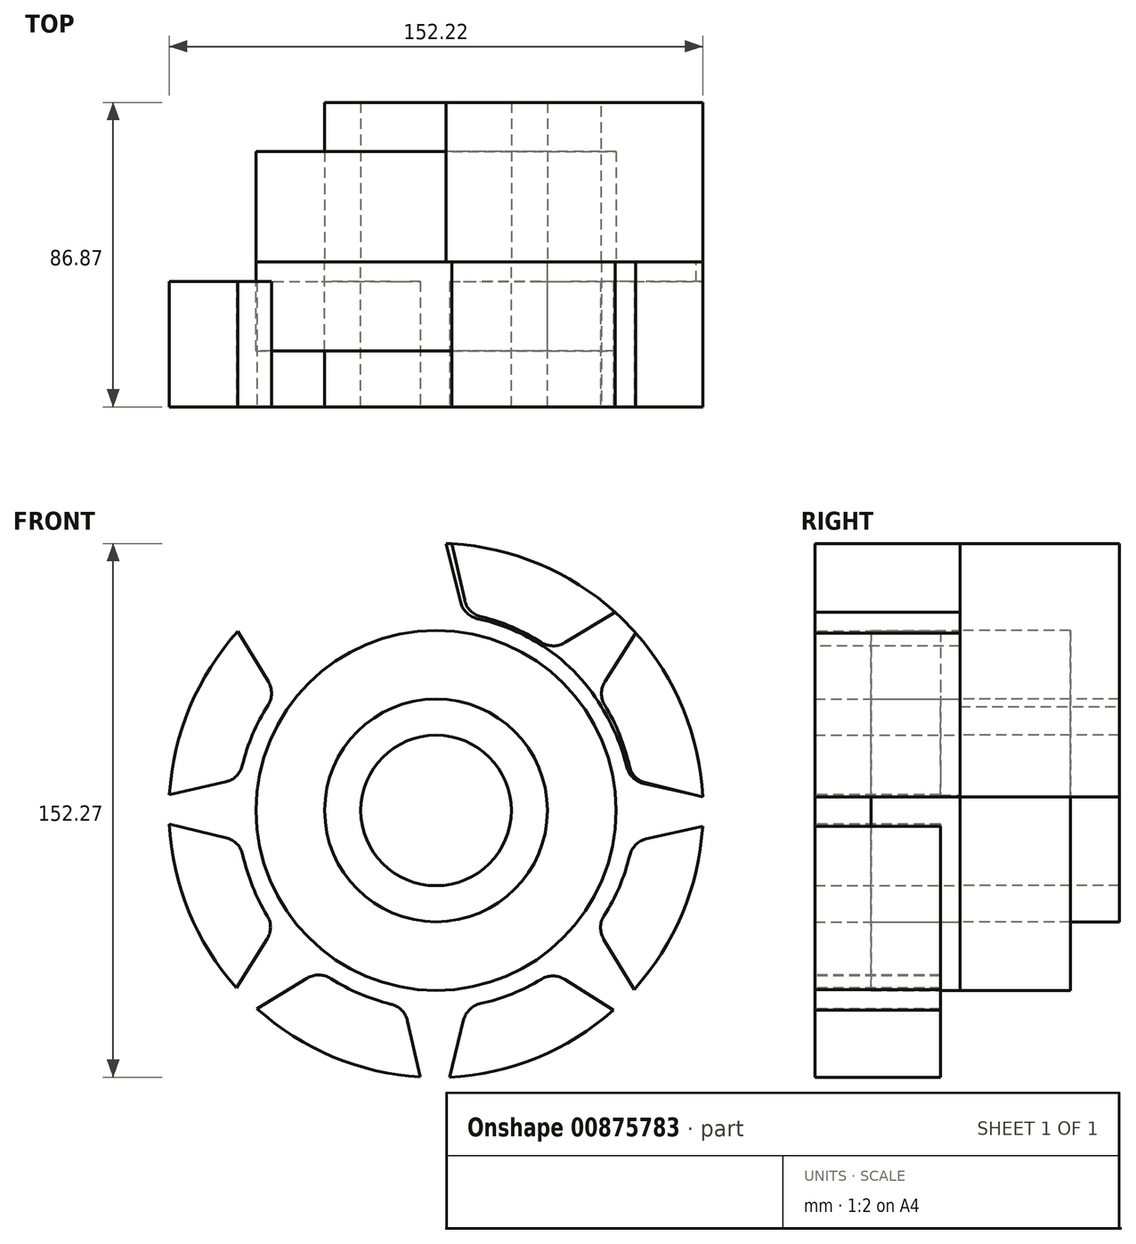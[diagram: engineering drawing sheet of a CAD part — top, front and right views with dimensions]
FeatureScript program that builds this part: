
annotation { "Feature Type Name" : "Feature", "Feature Type Description" : "" }
export const myFeature = defineFeature(function(context is Context, id is Id, definition is map)
    precondition{}
    {
        {
            var Q0;
            Q0=qCreatedBy(makeId("Front.planeOp"),FACE);
            var sketch = newSketch(context, id + "F0", { "sketchPlane" : qUnion([Q0])});
            skCircle(sketch, "E0", {"center": v(0, 0) * mm, "radius": 76.21 * mm});
            skCircle(sketch, "E1", {"center": v(0, 0) * mm, "radius": 31.78 * mm});
            skCircle(sketch, "E2", {"center": v(0, 0) * mm, "radius": 21.48 * mm});
            skCircle(sketch, "E3", {"center": v(0, 0) * mm, "radius": 51.35 * mm});
            skSolve(sketch);
        }
        {
            var Q0;
            Q0 = qSketchRegion(id + "F0", true);
            var Q1;
            Q1=makeQuery(id+"F0.imprint","IMPRINT",FACE,{"disambiguationData":[TD([[makeQuery(id+"F0.imprint","IMPRINT",EDGE,{"derivedFrom":sQuery(id+"F0.wireOp",EDGE,"E1")}),1.0]])]});
            extrude(context, id + "F1", {"entities" : qUnion([Q0, Q1]), "depth" : 41.4 * mm, "offsetDistance" : 25.4 * mm});
        }
        {
            var Q0;
            Q0=makeQuery(id+"F0.imprint","IMPRINT",FACE,{"disambiguationData":[TD([[makeQuery(id+"F0.imprint","IMPRINT",EDGE,{"derivedFrom":sQuery(id+"F0.wireOp",EDGE,"E1")}),-1.0]])]});
            extrude(context, id + "F2", {"entities" : qUnion([Q0]), "depth" : 25.4 * mm, "offsetDistance" : 25.4 * mm});
        }
        {
            var Q0;
            Q0=makeQuery(id+"F1.opExtrude","CAP_FACE",FACE,{"disambiguationData":[OSD([sQuery(id+"F0.wireOp",EDGE,"2gCDkCEJ-HWgE-DsvB-Vvop-13Bm3h3RxIBW"),sQuery(id+"F0.wireOp",EDGE,"E0")])],"isStart":false});
            var sketch = newSketch(context, id + "F3", { "sketchPlane" : qUnion([Q0])});
            skLineSegment(sketch, "E4", {"start": v(-3.86, 76.11) * mm, "end": v(-7.87, 59.83) * mm});
            skLineSegment(sketch, "E5.MirrorCS", {"start": v(-50.88, 57.18) * mm, "end": v(-36.71, 48.21) * mm});
            skArc(sketch, "E6", {"start": v(-30, 48.16) * mm, "mid": v(-21.63, 52.37) * mm, "end": v(-12.67, 55.14) * mm});
            skPoint(sketch, "E7.visualSharp", {"position": v(-33.24, 46.02) * mm});
            skArc(sketch, "E7.filletArc", {"start": v(-36.71, 48.21) * mm, "mid": v(-33.36, 47.23) * mm, "end": v(-30, 48.16) * mm});
            skPoint(sketch, "E8.visualSharp", {"position": v(-8.85, 55.84) * mm});
            skArc(sketch, "E8.filletArc", {"start": v(-12.67, 55.14) * mm, "mid": v(-9.6, 56.8) * mm, "end": v(-7.87, 59.83) * mm});
            skArc(sketch, "E9.1.0", {"start": v(-55.27, 12.84) * mm, "mid": v(-52.33, 21.74) * mm, "end": v(-47.95, 30.03) * mm});
            skArc(sketch, "E9.1.1", {"start": v(-60.05, 8.13) * mm, "mid": v(-56.99, 9.8) * mm, "end": v(-55.27, 12.84) * mm});
            skLineSegment(sketch, "E9.1.2", {"start": v(-76.41, 4.45) * mm, "end": v(-60.05, 8.13) * mm});
            skArc(sketch, "E9.1.3", {"start": v(-47.95, 30.03) * mm, "mid": v(-46.95, 33.37) * mm, "end": v(-47.87, 36.74) * mm});
            skLineSegment(sketch, "E9.1.4", {"start": v(-56.55, 51.09) * mm, "end": v(-47.87, 36.74) * mm});
            skArc(sketch, "E9.2.0", {"start": v(-48.16, -30) * mm, "mid": v(-52.37, -21.63) * mm, "end": v(-55.14, -12.67) * mm});
            skArc(sketch, "E9.2.1", {"start": v(-48.21, -36.71) * mm, "mid": v(-47.23, -33.36) * mm, "end": v(-48.16, -30) * mm});
            skLineSegment(sketch, "E9.2.2", {"start": v(-57.18, -50.88) * mm, "end": v(-48.21, -36.71) * mm});
            skArc(sketch, "E9.2.3", {"start": v(-55.14, -12.67) * mm, "mid": v(-56.8, -9.6) * mm, "end": v(-59.83, -7.87) * mm});
            skLineSegment(sketch, "E9.2.4", {"start": v(-76.11, -3.86) * mm, "end": v(-59.83, -7.87) * mm});
            skArc(sketch, "E9.3.0", {"start": v(-12.84, -55.27) * mm, "mid": v(-21.74, -52.33) * mm, "end": v(-30.03, -47.95) * mm});
            skArc(sketch, "E9.3.1", {"start": v(-8.13, -60.05) * mm, "mid": v(-9.8, -56.99) * mm, "end": v(-12.84, -55.27) * mm});
            skLineSegment(sketch, "E9.3.2", {"start": v(-4.45, -76.41) * mm, "end": v(-8.13, -60.05) * mm});
            skArc(sketch, "E9.3.3", {"start": v(-30.03, -47.95) * mm, "mid": v(-33.37, -46.95) * mm, "end": v(-36.74, -47.87) * mm});
            skLineSegment(sketch, "E9.3.4", {"start": v(-51.09, -56.55) * mm, "end": v(-36.74, -47.87) * mm});
            skArc(sketch, "E9.4.0", {"start": v(30, -48.16) * mm, "mid": v(21.63, -52.37) * mm, "end": v(12.67, -55.14) * mm});
            skArc(sketch, "E9.4.1", {"start": v(36.71, -48.21) * mm, "mid": v(33.36, -47.23) * mm, "end": v(30, -48.16) * mm});
            skLineSegment(sketch, "E9.4.2", {"start": v(50.88, -57.18) * mm, "end": v(36.71, -48.21) * mm});
            skArc(sketch, "E9.4.3", {"start": v(12.67, -55.14) * mm, "mid": v(9.6, -56.8) * mm, "end": v(7.87, -59.83) * mm});
            skLineSegment(sketch, "E9.4.4", {"start": v(3.86, -76.11) * mm, "end": v(7.87, -59.83) * mm});
            skArc(sketch, "E9.5.0", {"start": v(55.27, -12.84) * mm, "mid": v(52.33, -21.74) * mm, "end": v(47.95, -30.03) * mm});
            skArc(sketch, "E9.5.1", {"start": v(60.05, -8.13) * mm, "mid": v(56.99, -9.8) * mm, "end": v(55.27, -12.84) * mm});
            skLineSegment(sketch, "E9.5.2", {"start": v(76.41, -4.45) * mm, "end": v(60.05, -8.13) * mm});
            skArc(sketch, "E9.5.3", {"start": v(47.95, -30.03) * mm, "mid": v(46.95, -33.37) * mm, "end": v(47.87, -36.74) * mm});
            skLineSegment(sketch, "E9.5.4", {"start": v(56.55, -51.09) * mm, "end": v(47.87, -36.74) * mm});
            skArc(sketch, "E9.6.0", {"start": v(48.16, 30) * mm, "mid": v(52.37, 21.63) * mm, "end": v(55.14, 12.67) * mm});
            skArc(sketch, "E9.6.1", {"start": v(48.21, 36.71) * mm, "mid": v(47.23, 33.36) * mm, "end": v(48.16, 30) * mm});
            skLineSegment(sketch, "E9.6.2", {"start": v(57.18, 50.88) * mm, "end": v(48.21, 36.71) * mm});
            skArc(sketch, "E9.6.3", {"start": v(55.14, 12.67) * mm, "mid": v(56.8, 9.6) * mm, "end": v(59.83, 7.87) * mm});
            skLineSegment(sketch, "E9.6.4", {"start": v(76.11, 3.86) * mm, "end": v(59.83, 7.87) * mm});
            skArc(sketch, "E9.7.0", {"start": v(12.84, 55.27) * mm, "mid": v(21.74, 52.33) * mm, "end": v(30.03, 47.95) * mm});
            skArc(sketch, "E9.7.1", {"start": v(8.13, 60.05) * mm, "mid": v(9.8, 56.99) * mm, "end": v(12.84, 55.27) * mm});
            skLineSegment(sketch, "E9.7.2", {"start": v(4.45, 76.41) * mm, "end": v(8.13, 60.05) * mm});
            skArc(sketch, "E9.7.3", {"start": v(30.03, 47.95) * mm, "mid": v(33.37, 46.95) * mm, "end": v(36.74, 47.87) * mm});
            skLineSegment(sketch, "E9.7.4", {"start": v(51.09, 56.55) * mm, "end": v(36.74, 47.87) * mm});
            skPoint(sketch, "E9.center", {"position": v(0, 0) * mm});
            skSolve(sketch);
        }
        {
            var Q0;
            Q0=makeQuery(id+"F3.imprint","IMPRINT",FACE,{"disambiguationData":[TD([[makeQuery(id+"F3.imprint","IMPRINT",EDGE,{"derivedFrom":sQuery(id+"F3.wireOp",EDGE,"E9.1.0")}),1.0]])]});
            var Q1;
            {var subQ4=sQuery(id+"F3.wireOp",EDGE,"E4");Q1=makeQuery(id+"F3.imprint","IMPRINT",FACE,{"disambiguationData":[TD([[makeQuery(id+"F3.imprint","IMPRINT",EDGE,{"derivedFrom":subQ4}),-1.0]])]});}
            var Q2;
            Q2=makeQuery(id+"F3.imprint","IMPRINT",FACE,{"disambiguationData":[TD([[makeQuery(id+"F3.imprint","IMPRINT",EDGE,{"derivedFrom":sQuery(id+"F3.wireOp",EDGE,"E9.7.0")}),1.0]])]});
            var Q3;
            Q3=makeQuery(id+"F3.imprint","IMPRINT",FACE,{"disambiguationData":[TD([[makeQuery(id+"F3.imprint","IMPRINT",EDGE,{"derivedFrom":sQuery(id+"F3.wireOp",EDGE,"E9.6.0")}),1.0]])]});
            var Q4;
            Q4=makeQuery(id+"F3.imprint","IMPRINT",FACE,{"disambiguationData":[TD([[makeQuery(id+"F3.imprint","IMPRINT",EDGE,{"derivedFrom":sQuery(id+"F3.wireOp",EDGE,"E9.5.0")}),1.0]])]});
            var Q5;
            Q5=makeQuery(id+"F3.imprint","IMPRINT",FACE,{"disambiguationData":[TD([[makeQuery(id+"F3.imprint","IMPRINT",EDGE,{"derivedFrom":sQuery(id+"F3.wireOp",EDGE,"E9.4.0")}),1.0]])]});
            var Q6;
            Q6=makeQuery(id+"F3.imprint","IMPRINT",FACE,{"disambiguationData":[TD([[makeQuery(id+"F3.imprint","IMPRINT",EDGE,{"derivedFrom":sQuery(id+"F3.wireOp",EDGE,"E9.3.0")}),1.0]])]});
            var Q7;
            Q7=makeQuery(id+"F3.imprint","IMPRINT",FACE,{"disambiguationData":[TD([[makeQuery(id+"F3.imprint","IMPRINT",EDGE,{"derivedFrom":sQuery(id+"F3.wireOp",EDGE,"E9.2.0")}),1.0]])]});
            extrude(context, id + "F4", {"entities" : qUnion([Q0, Q1, Q2, Q3, Q4, Q5, Q6, Q7]), "operationType" : NewBodyOperationType.REMOVE, "oppositeDirection" : true, "depth" : 71.88 * mm, "offsetDistance" : 25.4 * mm});
        }
        {
            var Q0;
            Q0=makeQuery(id+"F0.imprint","IMPRINT",FACE,{"disambiguationData":[TD([[makeQuery(id+"F0.imprint","IMPRINT",EDGE,{"derivedFrom":sQuery(id+"F0.wireOp",EDGE,"E1")}),1.0]])]});
            var Q1;
            Q1=makeQuery(id+"F0.imprint","IMPRINT",FACE,{"disambiguationData":[TD([[makeQuery(id+"F0.imprint","IMPRINT",EDGE,{"derivedFrom":sQuery(id+"F0.wireOp",EDGE,"E0")}),1.0]])]});
            extrude(context, id + "F5", {"entities" : qUnion([Q0, Q1]), "oppositeDirection" : true, "depth" : 45.47 * mm, "offsetDistance" : 25.4 * mm});
        }
        {
            var Q0;
            Q0=makeQuery(id+"F0.imprint","IMPRINT",FACE,{"disambiguationData":[TD([[makeQuery(id+"F0.imprint","IMPRINT",EDGE,{"derivedFrom":sQuery(id+"F0.wireOp",EDGE,"E1")}),-1.0]])]});
            extrude(context, id + "F6", {"entities" : qUnion([Q0]), "oppositeDirection" : true, "depth" : 31.5 * mm, "offsetDistance" : 25.4 * mm});
        }
        {
            var Q0;
            Q0=makeQuery(id+"F5.opExtrude","CAP_FACE",FACE,{"disambiguationData":[OSD([sQuery(id+"F0.wireOp",EDGE,"E0"),sQuery(id+"F0.wireOp",EDGE,"E3")])],"isStart":false});
            var sketch = newSketch(context, id + "F7", { "sketchPlane" : qUnion([Q0])});
            skArc(sketch, "E10", {"start": v(-29.17, 47.74) * mm, "mid": v(-20.8, 51.95) * mm, "end": v(-11.84, 54.71) * mm});
            skPoint(sketch, "E11.visualSharp", {"position": v(-8.02, 55.41) * mm});
            skArc(sketch, "E11.filletArc", {"start": v(-11.84, 54.71) * mm, "mid": v(-8.77, 56.37) * mm, "end": v(-7.04, 59.4) * mm});
            skArc(sketch, "E12.1.0", {"start": v(-54.44, 12.42) * mm, "mid": v(-51.5, 21.31) * mm, "end": v(-47.12, 29.6) * mm});
            skArc(sketch, "E12.1.1", {"start": v(-59.22, 7.7) * mm, "mid": v(-56.15, 9.38) * mm, "end": v(-54.44, 12.42) * mm});
            skArc(sketch, "E13", {"start": v(-29.17, 47.74) * mm, "mid": v(-39.25, 39.76) * mm, "end": v(-47.12, 29.6) * mm});
            skPoint(sketch, "E14.center", {"position": v(0, 0) * mm});
            skLineSegment(sketch, "E15", {"start": v(-76.11, 3.9) * mm, "end": v(-59.22, 7.7) * mm});
            skLineSegment(sketch, "E16", {"start": v(-2.92, 76.16) * mm, "end": v(-7.04, 59.4) * mm});
            skLineSegment(sketch, "E17.1.0", {"start": v(-76.16, -2.92) * mm, "end": v(-59.4, -7.04) * mm});
            skArc(sketch, "E17.1.1", {"start": v(-47.74, -29.17) * mm, "mid": v(-51.95, -20.8) * mm, "end": v(-54.71, -11.84) * mm});
            skArc(sketch, "E17.1.2", {"start": v(-54.71, -11.84) * mm, "mid": v(-56.37, -8.77) * mm, "end": v(-59.4, -7.04) * mm});
            skArc(sketch, "E17.1.3", {"start": v(-47.74, -29.17) * mm, "mid": v(-39.76, -39.25) * mm, "end": v(-29.6, -47.12) * mm});
            skLineSegment(sketch, "E17.1.4", {"start": v(-3.9, -76.11) * mm, "end": v(-7.7, -59.22) * mm});
            skArc(sketch, "E17.1.5", {"start": v(-12.42, -54.44) * mm, "mid": v(-21.31, -51.5) * mm, "end": v(-29.6, -47.12) * mm});
            skArc(sketch, "E17.1.6", {"start": v(-7.7, -59.22) * mm, "mid": v(-9.38, -56.15) * mm, "end": v(-12.42, -54.44) * mm});
            skLineSegment(sketch, "E17.2.0", {"start": v(2.92, -76.16) * mm, "end": v(7.04, -59.4) * mm});
            skArc(sketch, "E17.2.1", {"start": v(29.17, -47.74) * mm, "mid": v(20.8, -51.95) * mm, "end": v(11.84, -54.71) * mm});
            skArc(sketch, "E17.2.2", {"start": v(11.84, -54.71) * mm, "mid": v(8.77, -56.37) * mm, "end": v(7.04, -59.4) * mm});
            skArc(sketch, "E17.2.3", {"start": v(29.17, -47.74) * mm, "mid": v(39.25, -39.76) * mm, "end": v(47.12, -29.6) * mm});
            skLineSegment(sketch, "E17.2.4", {"start": v(76.11, -3.9) * mm, "end": v(59.22, -7.7) * mm});
            skArc(sketch, "E17.2.5", {"start": v(54.44, -12.42) * mm, "mid": v(51.5, -21.31) * mm, "end": v(47.12, -29.6) * mm});
            skArc(sketch, "E17.2.6", {"start": v(59.22, -7.7) * mm, "mid": v(56.15, -9.38) * mm, "end": v(54.44, -12.42) * mm});
            skLineSegment(sketch, "E17.3.0", {"start": v(76.16, 2.92) * mm, "end": v(59.4, 7.04) * mm});
            skArc(sketch, "E17.3.1", {"start": v(47.74, 29.17) * mm, "mid": v(51.95, 20.8) * mm, "end": v(54.71, 11.84) * mm});
            skArc(sketch, "E17.3.2", {"start": v(54.71, 11.84) * mm, "mid": v(56.37, 8.77) * mm, "end": v(59.4, 7.04) * mm});
            skArc(sketch, "E17.3.3", {"start": v(47.74, 29.17) * mm, "mid": v(39.76, 39.25) * mm, "end": v(29.6, 47.12) * mm});
            skLineSegment(sketch, "E17.3.4", {"start": v(3.9, 76.11) * mm, "end": v(7.7, 59.22) * mm});
            skArc(sketch, "E17.3.5", {"start": v(12.42, 54.44) * mm, "mid": v(21.31, 51.5) * mm, "end": v(29.6, 47.12) * mm});
            skArc(sketch, "E17.3.6", {"start": v(7.7, 59.22) * mm, "mid": v(9.38, 56.15) * mm, "end": v(12.42, 54.44) * mm});
            skSolve(sketch);
        }
        {
            var Q0;
            Q0=makeQuery(id+"F7.imprint","IMPRINT",FACE,{"disambiguationData":[TD([[makeQuery(id+"F7.imprint","IMPRINT",EDGE,{"derivedFrom":sQuery(id+"F7.wireOp",EDGE,"E10")}),1.0]])]});
            var Q1;
            {var subQ0=sQuery(id+"F7.wireOp",EDGE,"E17.3.0");Q1=makeQuery(id+"F7.imprint","IMPRINT",FACE,{"disambiguationData":[TD([[makeQuery(id+"F7.imprint","IMPRINT",EDGE,{"derivedFrom":subQ0}),-1.0]])]});}
            var Q2;
            {var subQ0=sQuery(id+"F7.wireOp",EDGE,"E17.2.0");Q2=makeQuery(id+"F7.imprint","IMPRINT",FACE,{"disambiguationData":[TD([[makeQuery(id+"F7.imprint","IMPRINT",EDGE,{"derivedFrom":subQ0}),-1.0]])]});}
            var Q3;
            {var subQ0=sQuery(id+"F7.wireOp",EDGE,"E17.1.0");Q3=makeQuery(id+"F7.imprint","IMPRINT",FACE,{"disambiguationData":[TD([[makeQuery(id+"F7.imprint","IMPRINT",EDGE,{"derivedFrom":subQ0}),-1.0]])]});}
            extrude(context, id + "F8", {"entities" : qUnion([Q0, Q1, Q2, Q3]), "operationType" : NewBodyOperationType.REMOVE, "oppositeDirection" : true, "depth" : 51.05 * mm, "offsetDistance" : 25.4 * mm});
        }
    });
